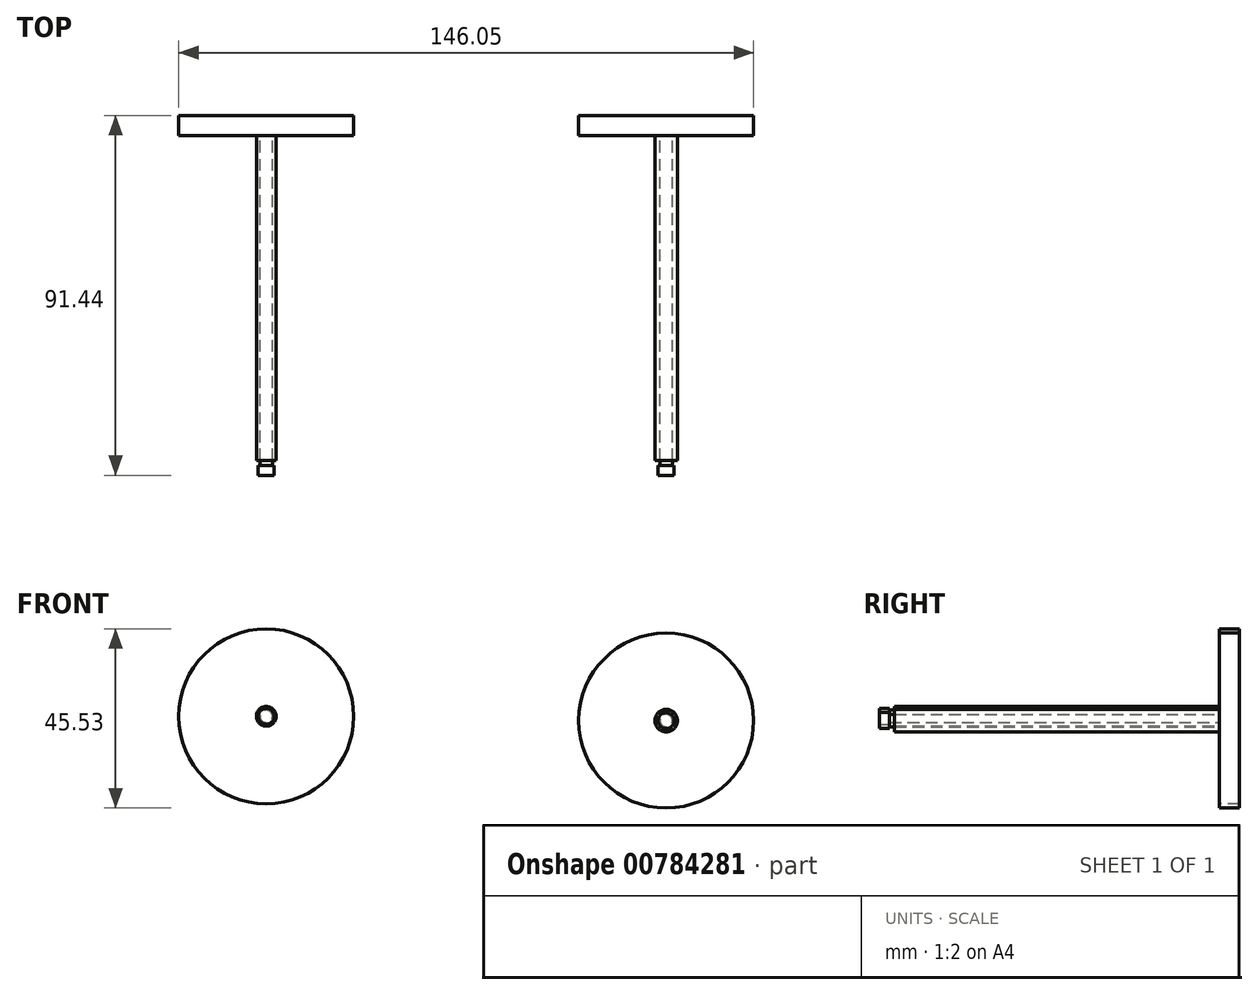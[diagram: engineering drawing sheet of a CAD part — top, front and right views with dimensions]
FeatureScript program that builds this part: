
annotation { "Feature Type Name" : "Feature", "Feature Type Description" : "" }
export const myFeature = defineFeature(function(context is Context, id is Id, definition is map)
    precondition{}
    {
        {
            var Q0;
            Q0=qCreatedBy(makeId("Front.planeOp"),FACE);
            var sketch = newSketch(context, id + "F0", { "sketchPlane" : qUnion([Q0])});
            skCircle(sketch, "E0", {"center": v(-90.16, 10.27) * mm, "radius": 2.5 * mm});
            skCircle(sketch, "E1", {"center": v(11.44, 9.19) * mm, "radius": 2.86 * mm});
            skSolve(sketch);
        }
        {
            var Q0;
            Q0 = qSketchRegion(id + "F0", true);
            extrude(context, id + "F1", {"entities" : qUnion([Q0]), "depth" : 82.55 * mm, "offsetDistance" : 25.4 * mm});
        }
        {
            var Q0;
            Q0=qCreatedBy(makeId("Front.planeOp"),FACE);
            var sketch = newSketch(context, id + "F2", { "sketchPlane" : qUnion([Q0])});
            skCircle(sketch, "E2", {"center": v(11.44, 9.19) * mm, "radius": 22.23 * mm});
            skPoint(sketch, "E3.center.orphan", {"position": v(-29.74, 10.26) * mm});
            skCircle(sketch, "E4", {"center": v(-90.16, 10.27) * mm, "radius": 22.23 * mm});
            skSolve(sketch);
        }
        {
            var Q0;
            Q0 = qSketchRegion(id + "F2", true);
            extrude(context, id + "F3", {"entities" : qUnion([Q0]), "oppositeDirection" : true, "depth" : 5.08 * mm, "offsetDistance" : 25.4 * mm});
        }
        {
            var Q0;
            Q0=qCreatedBy(makeId("Front.planeOp"),FACE);
            var sketch = newSketch(context, id + "F4", { "sketchPlane" : qUnion([Q0])});
            skCircle(sketch, "E5", {"center": v(-90.16, 10.27) * mm, "radius": 1.59 * mm});
            skCircle(sketch, "E6", {"center": v(11.44, 9.19) * mm, "radius": 1.59 * mm});
            skSolve(sketch);
        }
        {
            var Q0;
            Q0 = qSketchRegion(id + "F4", true);
            extrude(context, id + "F5", {"entities" : qUnion([Q0]), "depth" : 83.82 * mm, "offsetDistance" : 25.4 * mm});
        }
        {
            var Q0;
            Q0=makeQuery(id+"F5.opExtrude","CAP_FACE",FACE,{"disambiguationData":[OSD([sQuery(id+"F4.wireOp",EDGE,"E5")])],"isStart":false});
            var sketch = newSketch(context, id + "F6", { "sketchPlane" : qUnion([Q0])});
            skCircle(sketch, "E7", {"center": v(-90.16, 10.27) * mm, "radius": 2.03 * mm});
            skSolve(sketch);
        }
        {
            var Q0;
            Q0 = qSketchRegion(id + "F6", true);
            extrude(context, id + "F7", {"entities" : qUnion([Q0]), "operationType" : NewBodyOperationType.ADD, "depth" : 2.54 * mm, "offsetDistance" : 25.4 * mm});
        }
        {
            var Q0;
            Q0=makeQuery(id+"F5.opExtrude","CAP_FACE",FACE,{"disambiguationData":[OSD([sQuery(id+"F4.wireOp",EDGE,"E6")])],"isStart":false});
            var sketch = newSketch(context, id + "F8", { "sketchPlane" : qUnion([Q0])});
            skCircle(sketch, "E8", {"center": v(11.44, 9.19) * mm, "radius": 2.03 * mm});
            skSolve(sketch);
        }
        {
            var Q0;
            Q0 = qSketchRegion(id + "F8", true);
            extrude(context, id + "F9", {"entities" : qUnion([Q0]), "operationType" : NewBodyOperationType.ADD, "depth" : 2.54 * mm, "offsetDistance" : 25.4 * mm});
        }
    });
